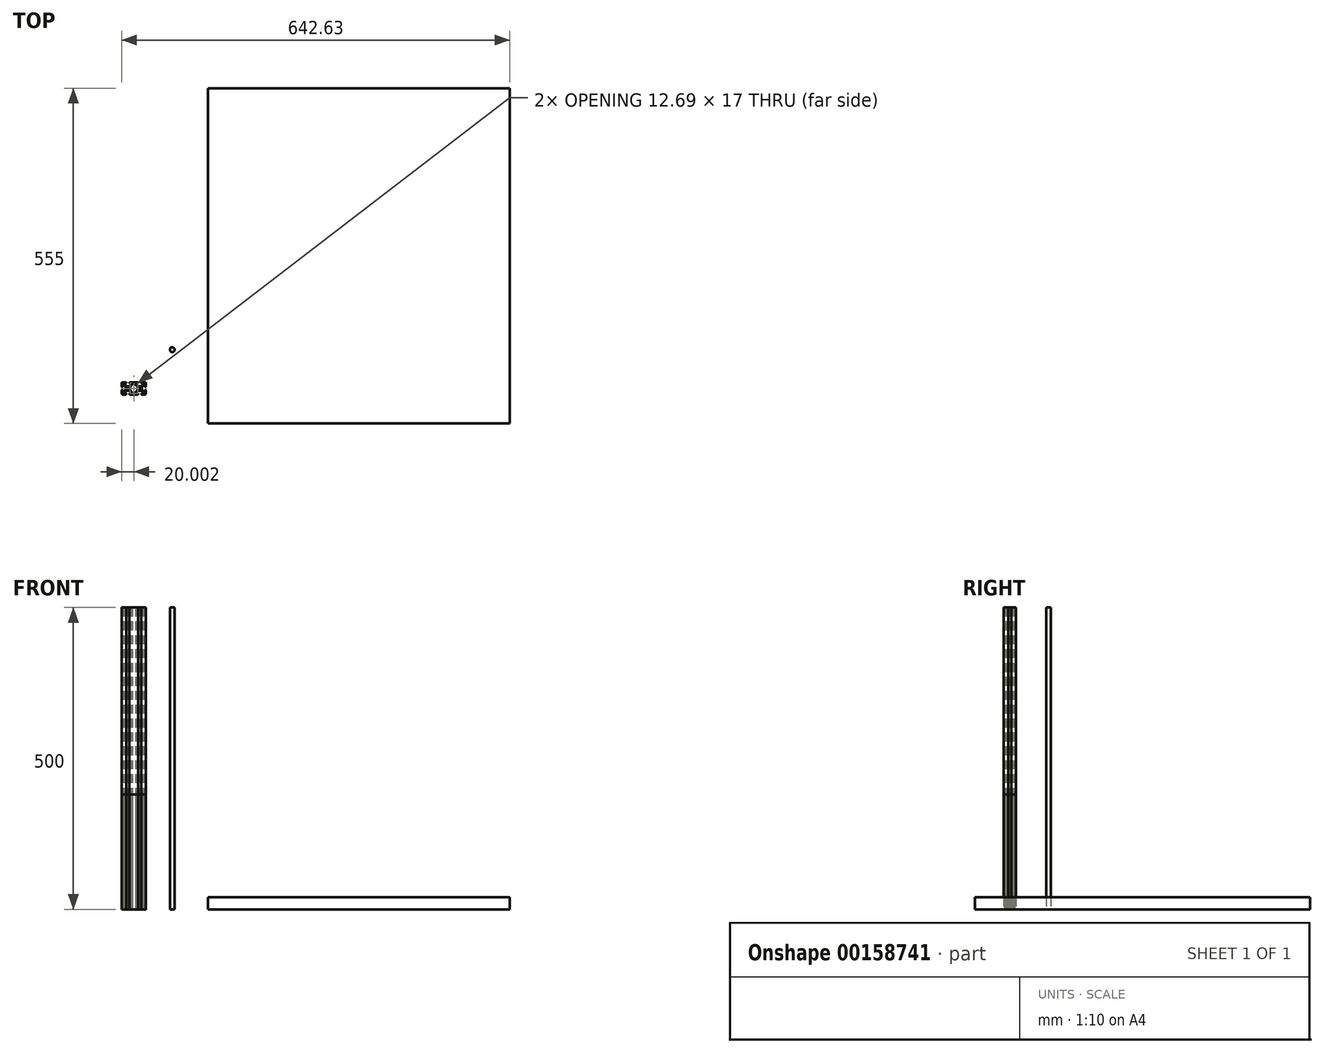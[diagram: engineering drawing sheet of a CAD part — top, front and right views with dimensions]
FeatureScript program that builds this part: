
annotation { "Feature Type Name" : "Feature", "Feature Type Description" : "" }
export const myFeature = defineFeature(function(context is Context, id is Id, definition is map)
    precondition{}
    {
        {
            var Q0;
            Q0=qCreatedBy(makeId("Top.planeOp"),FACE);
            var sketch = newSketch(context, id + "F0", { "sketchPlane" : qUnion([Q0])});
            skArc(sketch, "E0", {"start": v(-82.2, -54.18) * mm, "mid": v(-83.27, -54.62) * mm, "end": v(-83.7, -55.68) * mm});
            skLineSegment(sketch, "E1", {"start": v(-82.2, -54.18) * mm, "end": v(-76.85, -54.18) * mm});
            skArc(sketch, "E2", {"start": v(-76.34, -54.7) * mm, "mid": v(-76.49, -54.33) * mm, "end": v(-76.85, -54.18) * mm});
            skLineSegment(sketch, "E3", {"start": v(-76.34, -54.7) * mm, "end": v(-76.34, -55.18) * mm});
            skArc(sketch, "E4", {"start": v(-76.85, -55.68) * mm, "mid": v(-76.49, -55.54) * mm, "end": v(-76.34, -55.18) * mm});
            skLineSegment(sketch, "E5", {"start": v(-76.85, -55.68) * mm, "end": v(-79.2, -55.68) * mm});
            skLineSegment(sketch, "E6", {"start": v(-79.7, -56.2) * mm, "end": v(-79.7, -56.92) * mm});
            skLineSegment(sketch, "E7", {"start": v(-79.55, -57.28) * mm, "end": v(-76.45, -60.38) * mm});
            skLineSegment(sketch, "E8", {"start": v(-76.1, -60.53) * mm, "end": v(-71.32, -60.53) * mm});
            skLineSegment(sketch, "E9", {"start": v(-77.51, -61.44) * mm, "end": v(-80.61, -58.34) * mm});
            skLineSegment(sketch, "E10", {"start": v(-80.97, -58.19) * mm, "end": v(-81.7, -58.19) * mm});
            skLineSegment(sketch, "E11", {"start": v(-82.2, -58.7) * mm, "end": v(-82.2, -61.05) * mm});
            skLineSegment(sketch, "E12", {"start": v(-82.72, -61.55) * mm, "end": v(-83.2, -61.55) * mm});
            skLineSegment(sketch, "E13", {"start": v(-83.7, -61.05) * mm, "end": v(-83.7, -55.68) * mm});
            skArc(sketch, "E14", {"start": v(-79.2, -55.68) * mm, "mid": v(-79.55, -55.83) * mm, "end": v(-79.7, -56.2) * mm});
            skArc(sketch, "E15", {"start": v(-79.7, -56.92) * mm, "mid": v(-79.66, -57.11) * mm, "end": v(-79.55, -57.28) * mm});
            skArc(sketch, "E16", {"start": v(-80.61, -58.34) * mm, "mid": v(-80.78, -58.23) * mm, "end": v(-80.97, -58.19) * mm});
            skArc(sketch, "E17", {"start": v(-81.7, -58.19) * mm, "mid": v(-82.06, -58.34) * mm, "end": v(-82.2, -58.7) * mm});
            skArc(sketch, "E18", {"start": v(-82.72, -61.55) * mm, "mid": v(-82.36, -61.4) * mm, "end": v(-82.2, -61.05) * mm});
            skArc(sketch, "E19", {"start": v(-83.7, -61.05) * mm, "mid": v(-83.56, -61.4) * mm, "end": v(-83.2, -61.55) * mm});
            skLineSegment(sketch, "E20", {"start": v(-77.36, -61.8) * mm, "end": v(-77.36, -66.57) * mm});
            skLineSegment(sketch, "E21", {"start": v(-77.51, -66.93) * mm, "end": v(-80.61, -70.03) * mm});
            skLineSegment(sketch, "E22", {"start": v(-80.97, -70.18) * mm, "end": v(-81.7, -70.18) * mm});
            skLineSegment(sketch, "E23", {"start": v(-82.2, -69.67) * mm, "end": v(-82.2, -67.32) * mm});
            skLineSegment(sketch, "E24", {"start": v(-76.1, -67.84) * mm, "end": v(-71.32, -67.84) * mm});
            skLineSegment(sketch, "E25", {"start": v(-70.96, -67.99) * mm, "end": v(-67.86, -71.1) * mm});
            skLineSegment(sketch, "E26", {"start": v(-68.22, -72.68) * mm, "end": v(-70.57, -72.68) * mm});
            skLineSegment(sketch, "E27", {"start": v(-76.85, -72.68) * mm, "end": v(-79.2, -72.68) * mm});
            skLineSegment(sketch, "E28", {"start": v(-79.7, -71.45) * mm, "end": v(-79.7, -72.18) * mm});
            skLineSegment(sketch, "E29", {"start": v(-79.55, -71.1) * mm, "end": v(-76.45, -67.99) * mm});
            skLineSegment(sketch, "E30", {"start": v(-82.2, -74.18) * mm, "end": v(-76.85, -74.18) * mm});
            skLineSegment(sketch, "E31", {"start": v(-83.7, -72.68) * mm, "end": v(-83.7, -67.32) * mm});
            skLineSegment(sketch, "E32", {"start": v(-83.2, -66.81) * mm, "end": v(-82.72, -66.81) * mm});
            skLineSegment(sketch, "E33", {"start": v(-70.96, -60.38) * mm, "end": v(-67.86, -57.28) * mm});
            skLineSegment(sketch, "E34", {"start": v(-68.22, -55.68) * mm, "end": v(-70.57, -55.68) * mm});
            skLineSegment(sketch, "E35", {"start": v(-67.71, -56.2) * mm, "end": v(-67.71, -56.92) * mm});
            skLineSegment(sketch, "E36", {"start": v(-71.08, -55.18) * mm, "end": v(-71.08, -54.7) * mm});
            skLineSegment(sketch, "E37", {"start": v(-70.57, -54.18) * mm, "end": v(-63.7, -54.18) * mm});
            skPoint(sketch, "E37.endSnap0", {"position": v(-63.7, -54.18) * mm});
            skLineSegment(sketch, "E38", {"start": v(-69.9, -61.44) * mm, "end": v(-66.36, -57.9) * mm});
            skLineSegment(sketch, "E39", {"start": v(-66.21, -56.2) * mm, "end": v(-66.21, -57.54) * mm});
            skLineSegment(sketch, "E40", {"start": v(-65.7, -55.68) * mm, "end": v(-63.7, -55.68) * mm});
            skLineSegment(sketch, "E41", {"start": v(-70.05, -61.8) * mm, "end": v(-70.05, -66.57) * mm});
            skLineSegment(sketch, "E42", {"start": v(-69.9, -66.93) * mm, "end": v(-66.36, -70.47) * mm});
            skLineSegment(sketch, "E43", {"start": v(-66.21, -70.83) * mm, "end": v(-66.21, -72.18) * mm});
            skLineSegment(sketch, "E44", {"start": v(-71.08, -73.68) * mm, "end": v(-71.08, -73.2) * mm});
            skLineSegment(sketch, "E45", {"start": v(-70.57, -74.18) * mm, "end": v(-63.7, -74.18) * mm});
            skArc(sketch, "E46", {"start": v(-70.57, -54.18) * mm, "mid": v(-70.93, -54.33) * mm, "end": v(-71.08, -54.7) * mm});
            skArc(sketch, "E47", {"start": v(-71.08, -55.18) * mm, "mid": v(-70.93, -55.54) * mm, "end": v(-70.57, -55.68) * mm});
            skArc(sketch, "E48", {"start": v(-67.71, -56.2) * mm, "mid": v(-67.86, -55.83) * mm, "end": v(-68.22, -55.68) * mm});
            skArc(sketch, "E49", {"start": v(-67.86, -57.28) * mm, "mid": v(-67.75, -57.11) * mm, "end": v(-67.71, -56.92) * mm});
            skArc(sketch, "E50", {"start": v(-71.32, -60.53) * mm, "mid": v(-71.13, -60.5) * mm, "end": v(-70.96, -60.38) * mm});
            skArc(sketch, "E51", {"start": v(-76.45, -60.38) * mm, "mid": v(-76.29, -60.5) * mm, "end": v(-76.1, -60.53) * mm});
            skArc(sketch, "E52", {"start": v(-77.36, -61.8) * mm, "mid": v(-77.4, -61.6) * mm, "end": v(-77.51, -61.44) * mm});
            skArc(sketch, "E53", {"start": v(-65.7, -55.68) * mm, "mid": v(-66.06, -55.83) * mm, "end": v(-66.21, -56.2) * mm});
            skArc(sketch, "E54", {"start": v(-66.36, -57.9) * mm, "mid": v(-66.25, -57.73) * mm, "end": v(-66.21, -57.54) * mm});
            skArc(sketch, "E55", {"start": v(-83.2, -66.81) * mm, "mid": v(-83.56, -66.96) * mm, "end": v(-83.7, -67.32) * mm});
            skArc(sketch, "E56", {"start": v(-82.2, -67.32) * mm, "mid": v(-82.36, -66.96) * mm, "end": v(-82.72, -66.81) * mm});
            skArc(sketch, "E57", {"start": v(-82.2, -69.67) * mm, "mid": v(-82.06, -70.03) * mm, "end": v(-81.7, -70.18) * mm});
            skArc(sketch, "E58", {"start": v(-80.97, -70.18) * mm, "mid": v(-80.78, -70.14) * mm, "end": v(-80.61, -70.03) * mm});
            skArc(sketch, "E59", {"start": v(-79.55, -71.1) * mm, "mid": v(-79.66, -71.26) * mm, "end": v(-79.7, -71.45) * mm});
            skArc(sketch, "E60", {"start": v(-76.1, -67.84) * mm, "mid": v(-76.29, -67.88) * mm, "end": v(-76.45, -67.99) * mm});
            skArc(sketch, "E61", {"start": v(-77.51, -66.93) * mm, "mid": v(-77.4, -66.76) * mm, "end": v(-77.36, -66.57) * mm});
            skArc(sketch, "E62", {"start": v(-83.7, -72.68) * mm, "mid": v(-83.27, -73.74) * mm, "end": v(-82.2, -74.18) * mm});
            skArc(sketch, "E63", {"start": v(-76.85, -74.18) * mm, "mid": v(-76.49, -74.04) * mm, "end": v(-76.34, -73.68) * mm});
            skArc(sketch, "E64", {"start": v(-79.7, -72.18) * mm, "mid": v(-79.55, -72.54) * mm, "end": v(-79.2, -72.68) * mm});
            skArc(sketch, "E65", {"start": v(-76.34, -73.2) * mm, "mid": v(-76.49, -72.83) * mm, "end": v(-76.85, -72.68) * mm});
            skLineSegment(sketch, "E66", {"start": v(-76.34, -73.2) * mm, "end": v(-76.34, -73.68) * mm});
            skArc(sketch, "E67", {"start": v(-70.57, -72.68) * mm, "mid": v(-70.93, -72.83) * mm, "end": v(-71.08, -73.2) * mm});
            skArc(sketch, "E68", {"start": v(-71.08, -73.68) * mm, "mid": v(-70.93, -74.04) * mm, "end": v(-70.57, -74.18) * mm});
            skArc(sketch, "E69", {"start": v(-67.71, -71.45) * mm, "mid": v(-67.75, -71.26) * mm, "end": v(-67.86, -71.1) * mm});
            skArc(sketch, "E70", {"start": v(-68.22, -72.68) * mm, "mid": v(-67.86, -72.54) * mm, "end": v(-67.71, -72.18) * mm});
            skLineSegment(sketch, "E71", {"start": v(-67.71, -71.45) * mm, "end": v(-67.71, -72.18) * mm});
            skArc(sketch, "E72", {"start": v(-66.21, -70.83) * mm, "mid": v(-66.25, -70.63) * mm, "end": v(-66.36, -70.47) * mm});
            skArc(sketch, "E73", {"start": v(-66.21, -72.18) * mm, "mid": v(-66.06, -72.54) * mm, "end": v(-65.7, -72.68) * mm});
            skLineSegment(sketch, "E74", {"start": v(-63.7, -72.68) * mm, "end": v(-65.7, -72.68) * mm});
            skArc(sketch, "E75", {"start": v(-70.96, -67.99) * mm, "mid": v(-71.13, -67.88) * mm, "end": v(-71.32, -67.84) * mm});
            skArc(sketch, "E76", {"start": v(-70.05, -66.57) * mm, "mid": v(-70.01, -66.76) * mm, "end": v(-69.9, -66.93) * mm});
            skArc(sketch, "E77", {"start": v(-76.01, -62.06) * mm, "mid": v(-76.21, -62.83) * mm, "end": v(-75.64, -63.38) * mm});
            skArc(sketch, "E78", {"start": v(-74.51, -62.25) * mm, "mid": v(-75.06, -61.68) * mm, "end": v(-75.83, -61.88) * mm});
            skArc(sketch, "E79", {"start": v(-72.9, -62.25) * mm, "mid": v(-73.7, -62.09) * mm, "end": v(-74.51, -62.25) * mm});
            skLineSegment(sketch, "E80", {"start": v(-76.01, -62.06) * mm, "end": v(-75.83, -61.88) * mm});
            skArc(sketch, "E81.1.0", {"start": v(-75.83, -66.49) * mm, "mid": v(-75.06, -66.7) * mm, "end": v(-74.51, -66.12) * mm});
            skArc(sketch, "E81.1.1", {"start": v(-75.64, -63.38) * mm, "mid": v(-75.8, -64.18) * mm, "end": v(-75.64, -64.99) * mm});
            skArc(sketch, "E81.1.2", {"start": v(-75.64, -64.99) * mm, "mid": v(-76.21, -65.54) * mm, "end": v(-76.01, -66.3) * mm});
            skLineSegment(sketch, "E81.1.3", {"start": v(-75.83, -66.49) * mm, "end": v(-76.01, -66.3) * mm});
            skArc(sketch, "E81.2.0", {"start": v(-71.4, -66.3) * mm, "mid": v(-71.2, -65.54) * mm, "end": v(-71.77, -64.99) * mm});
            skArc(sketch, "E81.2.1", {"start": v(-74.51, -66.12) * mm, "mid": v(-73.7, -66.28) * mm, "end": v(-72.9, -66.12) * mm});
            skArc(sketch, "E81.2.2", {"start": v(-72.9, -66.12) * mm, "mid": v(-72.35, -66.7) * mm, "end": v(-71.58, -66.49) * mm});
            skLineSegment(sketch, "E81.2.3", {"start": v(-71.4, -66.3) * mm, "end": v(-71.58, -66.49) * mm});
            skArc(sketch, "E81.3.0", {"start": v(-71.58, -61.88) * mm, "mid": v(-72.35, -61.68) * mm, "end": v(-72.9, -62.25) * mm});
            skArc(sketch, "E81.3.1", {"start": v(-71.77, -64.99) * mm, "mid": v(-71.61, -64.18) * mm, "end": v(-71.77, -63.38) * mm});
            skArc(sketch, "E81.3.2", {"start": v(-71.77, -63.38) * mm, "mid": v(-71.2, -62.83) * mm, "end": v(-71.4, -62.06) * mm});
            skLineSegment(sketch, "E81.3.3", {"start": v(-71.58, -61.88) * mm, "end": v(-71.4, -62.06) * mm});
            skLineSegment(sketch, "E82.MirrorCS", {"start": v(-51.08, -73.2) * mm, "end": v(-51.08, -73.68) * mm});
            skLineSegment(sketch, "E83.MirrorCS", {"start": v(-56.01, -66.3) * mm, "end": v(-55.83, -66.49) * mm});
            skLineSegment(sketch, "E84.MirrorCS", {"start": v(-51.4, -62.06) * mm, "end": v(-51.58, -61.88) * mm});
            skLineSegment(sketch, "E85.MirrorCS", {"start": v(-59.7, -71.45) * mm, "end": v(-59.7, -72.18) * mm});
            skArc(sketch, "E86.MirrorCS", {"start": v(-54.51, -66.12) * mm, "mid": v(-55.06, -66.7) * mm, "end": v(-55.83, -66.49) * mm});
            skLineSegment(sketch, "E87.MirrorCS", {"start": v(-47.71, -56.2) * mm, "end": v(-47.71, -56.92) * mm});
            skLineSegment(sketch, "E88.MirrorCS", {"start": v(-51.08, -54.7) * mm, "end": v(-51.08, -55.18) * mm});
            skArc(sketch, "E89.MirrorCS", {"start": v(-51.08, -54.7) * mm, "mid": v(-50.93, -54.33) * mm, "end": v(-50.57, -54.18) * mm});
            skArc(sketch, "E90.MirrorCS", {"start": v(-47.71, -56.92) * mm, "mid": v(-47.75, -57.11) * mm, "end": v(-47.86, -57.28) * mm});
            skArc(sketch, "E91.MirrorCS", {"start": v(-59.2, -72.68) * mm, "mid": v(-59.55, -72.54) * mm, "end": v(-59.7, -72.18) * mm});
            skArc(sketch, "E92.MirrorCS", {"start": v(-50.57, -74.18) * mm, "mid": v(-50.93, -74.04) * mm, "end": v(-51.08, -73.68) * mm});
            skArc(sketch, "E93.MirrorCS", {"start": v(-61.71, -55.68) * mm, "mid": v(-61.35, -55.83) * mm, "end": v(-61.2, -56.2) * mm});
            skArc(sketch, "E94.MirrorCS", {"start": v(-59.7, -71.45) * mm, "mid": v(-59.66, -71.26) * mm, "end": v(-59.55, -71.1) * mm});
            skArc(sketch, "E95.MirrorCS", {"start": v(-56.01, -66.3) * mm, "mid": v(-56.21, -65.54) * mm, "end": v(-55.64, -64.99) * mm});
            skLineSegment(sketch, "E96.MirrorCS", {"start": v(-55.83, -61.88) * mm, "end": v(-56.01, -62.06) * mm});
            skLineSegment(sketch, "E97.MirrorCS", {"start": v(-56.34, -73.68) * mm, "end": v(-56.34, -73.2) * mm});
            skArc(sketch, "E98.MirrorCS", {"start": v(-56.34, -73.68) * mm, "mid": v(-56.49, -74.04) * mm, "end": v(-56.85, -74.18) * mm});
            skArc(sketch, "E99.MirrorCS", {"start": v(-56.45, -67.99) * mm, "mid": v(-56.29, -67.88) * mm, "end": v(-56.1, -67.84) * mm});
            skLineSegment(sketch, "E100.MirrorCS", {"start": v(-59.2, -55.68) * mm, "end": v(-56.85, -55.68) * mm});
            skArc(sketch, "E101.MirrorCS", {"start": v(-56.1, -60.53) * mm, "mid": v(-56.29, -60.5) * mm, "end": v(-56.45, -60.38) * mm});
            skArc(sketch, "E102.MirrorCS", {"start": v(-51.77, -63.38) * mm, "mid": v(-51.61, -64.18) * mm, "end": v(-51.77, -64.99) * mm});
            skArc(sketch, "E103.MirrorCS", {"start": v(-44.7, -61.55) * mm, "mid": v(-45.06, -61.4) * mm, "end": v(-45.2, -61.05) * mm});
            skArc(sketch, "E104.MirrorCS", {"start": v(-61.2, -72.18) * mm, "mid": v(-61.35, -72.54) * mm, "end": v(-61.71, -72.68) * mm});
            skArc(sketch, "E105.MirrorCS", {"start": v(-55.83, -61.88) * mm, "mid": v(-55.06, -61.68) * mm, "end": v(-54.51, -62.25) * mm});
            skArc(sketch, "E106.MirrorCS", {"start": v(-45.2, -69.67) * mm, "mid": v(-45.36, -70.03) * mm, "end": v(-45.72, -70.18) * mm});
            skArc(sketch, "E107.MirrorCS", {"start": v(-59.55, -57.28) * mm, "mid": v(-59.66, -57.11) * mm, "end": v(-59.7, -56.92) * mm});
            skArc(sketch, "E108.MirrorCS", {"start": v(-51.08, -73.2) * mm, "mid": v(-50.93, -72.83) * mm, "end": v(-50.57, -72.68) * mm});
            skArc(sketch, "E109.MirrorCS", {"start": v(-51.58, -66.49) * mm, "mid": v(-52.35, -66.7) * mm, "end": v(-52.9, -66.12) * mm});
            skArc(sketch, "E110.MirrorCS", {"start": v(-45.72, -58.19) * mm, "mid": v(-45.36, -58.34) * mm, "end": v(-45.2, -58.7) * mm});
            skArc(sketch, "E111.MirrorCS", {"start": v(-61.2, -70.83) * mm, "mid": v(-61.16, -70.63) * mm, "end": v(-61.05, -70.47) * mm});
            skLineSegment(sketch, "E112.MirrorCS", {"start": v(-61.71, -55.68) * mm, "end": v(-63.7, -55.68) * mm});
            skArc(sketch, "E113.MirrorCS", {"start": v(-45.2, -67.32) * mm, "mid": v(-45.06, -66.96) * mm, "end": v(-44.7, -66.81) * mm});
            skLineSegment(sketch, "E114.MirrorCS", {"start": v(-44.22, -66.81) * mm, "end": v(-44.7, -66.81) * mm});
            skArc(sketch, "E115.MirrorCS", {"start": v(-59.7, -56.2) * mm, "mid": v(-59.55, -55.83) * mm, "end": v(-59.2, -55.68) * mm});
            skArc(sketch, "E116.MirrorCS", {"start": v(-47.71, -72.18) * mm, "mid": v(-47.86, -72.54) * mm, "end": v(-48.22, -72.68) * mm});
            skArc(sketch, "E117.MirrorCS", {"start": v(-46.8, -58.34) * mm, "mid": v(-46.64, -58.23) * mm, "end": v(-46.44, -58.19) * mm});
            skLineSegment(sketch, "E118.MirrorCS", {"start": v(-45.2, -69.67) * mm, "end": v(-45.2, -67.32) * mm});
            skLineSegment(sketch, "E119.MirrorCS", {"start": v(-61.2, -56.2) * mm, "end": v(-61.2, -57.54) * mm});
            skArc(sketch, "E120.MirrorCS", {"start": v(-44.22, -66.81) * mm, "mid": v(-43.86, -66.96) * mm, "end": v(-43.7, -67.32) * mm});
            skLineSegment(sketch, "E121.MirrorCS", {"start": v(-44.7, -61.55) * mm, "end": v(-44.22, -61.55) * mm});
            skLineSegment(sketch, "E122.MirrorCS", {"start": v(-46.44, -58.19) * mm, "end": v(-45.72, -58.19) * mm});
            skArc(sketch, "E123.MirrorCS", {"start": v(-50.57, -55.68) * mm, "mid": v(-50.93, -55.54) * mm, "end": v(-51.08, -55.18) * mm});
            skArc(sketch, "E124.MirrorCS", {"start": v(-45.2, -54.18) * mm, "mid": v(-44.15, -54.62) * mm, "end": v(-43.7, -55.68) * mm});
            skArc(sketch, "E125.MirrorCS", {"start": v(-48.22, -55.68) * mm, "mid": v(-47.86, -55.83) * mm, "end": v(-47.71, -56.2) * mm});
            skArc(sketch, "E126.MirrorCS", {"start": v(-61.05, -57.9) * mm, "mid": v(-61.16, -57.73) * mm, "end": v(-61.2, -57.54) * mm});
            skArc(sketch, "E127.MirrorCS", {"start": v(-56.34, -55.18) * mm, "mid": v(-56.49, -55.54) * mm, "end": v(-56.85, -55.68) * mm});
            skArc(sketch, "E128.MirrorCS", {"start": v(-54.51, -62.25) * mm, "mid": v(-53.7, -62.09) * mm, "end": v(-52.9, -62.25) * mm});
            skArc(sketch, "E129.MirrorCS", {"start": v(-52.9, -66.12) * mm, "mid": v(-53.7, -66.28) * mm, "end": v(-54.51, -66.12) * mm});
            skLineSegment(sketch, "E130.MirrorCS", {"start": v(-46.44, -70.18) * mm, "end": v(-45.72, -70.18) * mm});
            skArc(sketch, "E131.MirrorCS", {"start": v(-56.85, -54.18) * mm, "mid": v(-56.49, -54.33) * mm, "end": v(-56.34, -54.7) * mm});
            skArc(sketch, "E132.MirrorCS", {"start": v(-43.7, -72.68) * mm, "mid": v(-44.15, -73.74) * mm, "end": v(-45.2, -74.18) * mm});
            skArc(sketch, "E133.MirrorCS", {"start": v(-52.9, -62.25) * mm, "mid": v(-52.35, -61.68) * mm, "end": v(-51.58, -61.88) * mm});
            skArc(sketch, "E134.MirrorCS", {"start": v(-57.36, -66.57) * mm, "mid": v(-57.4, -66.76) * mm, "end": v(-57.51, -66.93) * mm});
            skLineSegment(sketch, "E135.MirrorCS", {"start": v(-47.71, -71.45) * mm, "end": v(-47.71, -72.18) * mm});
            skArc(sketch, "E136.MirrorCS", {"start": v(-51.32, -67.84) * mm, "mid": v(-51.13, -67.88) * mm, "end": v(-50.96, -67.99) * mm});
            skLineSegment(sketch, "E137.MirrorCS", {"start": v(-56.34, -55.18) * mm, "end": v(-56.34, -54.7) * mm});
            skArc(sketch, "E138.MirrorCS", {"start": v(-50.05, -61.8) * mm, "mid": v(-50.01, -61.6) * mm, "end": v(-49.9, -61.44) * mm});
            skArc(sketch, "E139.MirrorCS", {"start": v(-49.9, -66.93) * mm, "mid": v(-50.01, -66.76) * mm, "end": v(-50.05, -66.57) * mm});
            skLineSegment(sketch, "E140.MirrorCS", {"start": v(-51.58, -66.49) * mm, "end": v(-51.4, -66.3) * mm});
            skArc(sketch, "E141.MirrorCS", {"start": v(-51.4, -62.06) * mm, "mid": v(-51.2, -62.83) * mm, "end": v(-51.77, -63.38) * mm});
            skArc(sketch, "E142.MirrorCS", {"start": v(-55.64, -63.38) * mm, "mid": v(-56.21, -62.83) * mm, "end": v(-56.01, -62.06) * mm});
            skLineSegment(sketch, "E143.MirrorCS", {"start": v(-61.2, -70.83) * mm, "end": v(-61.2, -72.18) * mm});
            skArc(sketch, "E144.MirrorCS", {"start": v(-47.86, -71.1) * mm, "mid": v(-47.75, -71.26) * mm, "end": v(-47.71, -71.45) * mm});
            skLineSegment(sketch, "E145.MirrorCS", {"start": v(-59.7, -56.2) * mm, "end": v(-59.7, -56.92) * mm});
            skArc(sketch, "E146.MirrorCS", {"start": v(-50.96, -60.38) * mm, "mid": v(-51.13, -60.5) * mm, "end": v(-51.32, -60.53) * mm});
            skArc(sketch, "E147.MirrorCS", {"start": v(-56.85, -72.68) * mm, "mid": v(-56.49, -72.83) * mm, "end": v(-56.34, -73.2) * mm});
            skArc(sketch, "E148.MirrorCS", {"start": v(-51.77, -64.99) * mm, "mid": v(-51.2, -65.54) * mm, "end": v(-51.4, -66.3) * mm});
            skArc(sketch, "E149.MirrorCS", {"start": v(-43.7, -61.05) * mm, "mid": v(-43.86, -61.4) * mm, "end": v(-44.22, -61.55) * mm});
            skLineSegment(sketch, "E150.MirrorCS", {"start": v(-63.7, -72.68) * mm, "end": v(-61.71, -72.68) * mm});
            skArc(sketch, "E151.MirrorCS", {"start": v(-55.64, -64.99) * mm, "mid": v(-55.8, -64.18) * mm, "end": v(-55.64, -63.38) * mm});
            skLineSegment(sketch, "E152.MirrorCS", {"start": v(-59.2, -72.68) * mm, "end": v(-56.85, -72.68) * mm});
            skArc(sketch, "E153.MirrorCS", {"start": v(-46.44, -70.18) * mm, "mid": v(-46.64, -70.14) * mm, "end": v(-46.8, -70.03) * mm});
            skLineSegment(sketch, "E154.MirrorCS", {"start": v(-56.45, -67.99) * mm, "end": v(-59.55, -71.1) * mm});
            skLineSegment(sketch, "E155.MirrorCS", {"start": v(-57.36, -61.8) * mm, "end": v(-57.36, -66.57) * mm});
            skLineSegment(sketch, "E156.MirrorCS", {"start": v(-56.45, -60.38) * mm, "end": v(-59.55, -57.28) * mm});
            skLineSegment(sketch, "E157.MirrorCS", {"start": v(-51.32, -67.84) * mm, "end": v(-56.1, -67.84) * mm});
            skLineSegment(sketch, "E158.MirrorCS", {"start": v(-45.2, -58.7) * mm, "end": v(-45.2, -61.05) * mm});
            skLineSegment(sketch, "E159.MirrorCS", {"start": v(-49.9, -61.44) * mm, "end": v(-46.8, -58.34) * mm});
            skLineSegment(sketch, "E160.MirrorCS", {"start": v(-51.32, -60.53) * mm, "end": v(-56.1, -60.53) * mm});
            skLineSegment(sketch, "E161.MirrorCS", {"start": v(-47.86, -57.28) * mm, "end": v(-50.96, -60.38) * mm});
            skLineSegment(sketch, "E162.MirrorCS", {"start": v(-50.57, -55.68) * mm, "end": v(-48.22, -55.68) * mm});
            skLineSegment(sketch, "E163.MirrorCS", {"start": v(-45.2, -54.18) * mm, "end": v(-50.57, -54.18) * mm});
            skLineSegment(sketch, "E164.MirrorCS", {"start": v(-43.7, -61.05) * mm, "end": v(-43.7, -55.68) * mm});
            skLineSegment(sketch, "E165.MirrorCS", {"start": v(-57.51, -61.44) * mm, "end": v(-61.05, -57.9) * mm});
            skLineSegment(sketch, "E166.MirrorCS", {"start": v(-43.7, -72.68) * mm, "end": v(-43.7, -67.32) * mm});
            skLineSegment(sketch, "E167.MirrorCS", {"start": v(-56.85, -54.18) * mm, "end": v(-63.7, -54.18) * mm});
            skLineSegment(sketch, "E168.MirrorCS", {"start": v(-45.2, -74.18) * mm, "end": v(-50.57, -74.18) * mm});
            skLineSegment(sketch, "E169.MirrorCS", {"start": v(-49.9, -66.93) * mm, "end": v(-46.8, -70.03) * mm});
            skLineSegment(sketch, "E170.MirrorCS", {"start": v(-47.86, -71.1) * mm, "end": v(-50.96, -67.99) * mm});
            skLineSegment(sketch, "E171.MirrorCS", {"start": v(-56.85, -74.18) * mm, "end": v(-63.7, -74.18) * mm});
            skLineSegment(sketch, "E172.MirrorCS", {"start": v(-50.05, -61.8) * mm, "end": v(-50.05, -66.57) * mm});
            skLineSegment(sketch, "E173.MirrorCS", {"start": v(-50.57, -72.68) * mm, "end": v(-48.22, -72.68) * mm});
            skLineSegment(sketch, "E174.MirrorCS", {"start": v(-57.51, -66.93) * mm, "end": v(-61.05, -70.47) * mm});
            skArc(sketch, "E175", {"start": v(-69.9, -61.44) * mm, "mid": v(-70.01, -61.6) * mm, "end": v(-70.05, -61.8) * mm});
            skArc(sketch, "E176", {"start": v(-57.36, -61.8) * mm, "mid": v(-57.4, -61.6) * mm, "end": v(-57.51, -61.44) * mm});
            skCircle(sketch, "E177", {"center": v(0, 0) * mm, "radius": 4 * mm});
            skArc(sketch, "E178", {"start": v(-19.39, -61.83) * mm, "mid": v(-20.45, -62.27) * mm, "end": v(-20.89, -63.33) * mm});
            skLineSegment(sketch, "E179", {"start": v(-19.39, -61.83) * mm, "end": v(-14.03, -61.83) * mm});
            skArc(sketch, "E180", {"start": v(-13.52, -62.34) * mm, "mid": v(-13.67, -61.98) * mm, "end": v(-14.03, -61.83) * mm});
            skLineSegment(sketch, "E181", {"start": v(-13.52, -62.34) * mm, "end": v(-13.52, -62.83) * mm});
            skArc(sketch, "E182", {"start": v(-14.03, -63.33) * mm, "mid": v(-13.67, -63.19) * mm, "end": v(-13.52, -62.83) * mm});
            skLineSegment(sketch, "E183", {"start": v(-14.03, -63.33) * mm, "end": v(-16.37, -63.33) * mm});
            skLineSegment(sketch, "E184", {"start": v(-16.88, -63.84) * mm, "end": v(-16.88, -64.57) * mm});
            skLineSegment(sketch, "E185", {"start": v(-16.73, -64.93) * mm, "end": v(-13.63, -68.03) * mm});
            skLineSegment(sketch, "E186", {"start": v(-13.27, -68.18) * mm, "end": v(-8.5, -68.18) * mm});
            skLineSegment(sketch, "E187", {"start": v(-14.7, -69.1) * mm, "end": v(-17.8, -65.99) * mm});
            skLineSegment(sketch, "E188", {"start": v(-18.15, -65.84) * mm, "end": v(-18.88, -65.84) * mm});
            skLineSegment(sketch, "E189", {"start": v(-19.39, -66.35) * mm, "end": v(-19.39, -68.7) * mm});
            skLineSegment(sketch, "E190", {"start": v(-19.9, -69.2) * mm, "end": v(-20.38, -69.2) * mm});
            skLineSegment(sketch, "E191", {"start": v(-20.89, -68.7) * mm, "end": v(-20.89, -63.33) * mm});
            skArc(sketch, "E192", {"start": v(-16.37, -63.33) * mm, "mid": v(-16.73, -63.48) * mm, "end": v(-16.88, -63.84) * mm});
            skArc(sketch, "E193", {"start": v(-16.88, -64.57) * mm, "mid": v(-16.84, -64.76) * mm, "end": v(-16.73, -64.93) * mm});
            skArc(sketch, "E194", {"start": v(-17.8, -65.99) * mm, "mid": v(-17.96, -65.88) * mm, "end": v(-18.15, -65.84) * mm});
            skArc(sketch, "E195", {"start": v(-18.88, -65.84) * mm, "mid": v(-19.24, -65.99) * mm, "end": v(-19.39, -66.35) * mm});
            skArc(sketch, "E196", {"start": v(-19.9, -69.2) * mm, "mid": v(-19.54, -69.06) * mm, "end": v(-19.39, -68.7) * mm});
            skArc(sketch, "E197", {"start": v(-20.89, -68.7) * mm, "mid": v(-20.74, -69.06) * mm, "end": v(-20.38, -69.2) * mm});
            skLineSegment(sketch, "E198", {"start": v(-14.54, -69.45) * mm, "end": v(-14.54, -74.22) * mm});
            skLineSegment(sketch, "E199", {"start": v(-14.7, -74.58) * mm, "end": v(-17.8, -77.68) * mm});
            skLineSegment(sketch, "E200", {"start": v(-18.15, -77.83) * mm, "end": v(-18.88, -77.83) * mm});
            skLineSegment(sketch, "E201", {"start": v(-19.39, -77.32) * mm, "end": v(-19.39, -74.97) * mm});
            skLineSegment(sketch, "E202", {"start": v(-13.27, -75.49) * mm, "end": v(-8.5, -75.49) * mm});
            skLineSegment(sketch, "E203", {"start": v(-8.14, -75.64) * mm, "end": v(-5.04, -78.74) * mm});
            skLineSegment(sketch, "E204", {"start": v(-5.4, -80.33) * mm, "end": v(-7.75, -80.33) * mm});
            skLineSegment(sketch, "E205", {"start": v(-14.03, -80.33) * mm, "end": v(-16.37, -80.33) * mm});
            skLineSegment(sketch, "E206", {"start": v(-16.88, -79.1) * mm, "end": v(-16.88, -79.83) * mm});
            skLineSegment(sketch, "E207", {"start": v(-16.73, -78.74) * mm, "end": v(-13.63, -75.64) * mm});
            skLineSegment(sketch, "E208", {"start": v(-19.39, -81.83) * mm, "end": v(-14.03, -81.83) * mm});
            skLineSegment(sketch, "E209", {"start": v(-20.89, -80.33) * mm, "end": v(-20.89, -74.97) * mm});
            skLineSegment(sketch, "E210", {"start": v(-20.38, -74.46) * mm, "end": v(-19.9, -74.46) * mm});
            skLineSegment(sketch, "E211", {"start": v(-8.14, -68.03) * mm, "end": v(-5.04, -64.93) * mm});
            skLineSegment(sketch, "E212", {"start": v(-5.4, -63.33) * mm, "end": v(-7.75, -63.33) * mm});
            skLineSegment(sketch, "E213", {"start": v(-4.9, -63.84) * mm, "end": v(-4.9, -64.57) * mm});
            skLineSegment(sketch, "E214", {"start": v(-8.26, -62.83) * mm, "end": v(-8.26, -62.34) * mm});
            skLineSegment(sketch, "E215", {"start": v(-7.75, -61.83) * mm, "end": v(-0.89, -61.83) * mm});
            skPoint(sketch, "E215.endSnap0", {"position": v(-0.89, -61.83) * mm});
            skLineSegment(sketch, "E216", {"start": v(-7.08, -69.1) * mm, "end": v(-3.54, -65.55) * mm});
            skLineSegment(sketch, "E217", {"start": v(-3.4, -63.84) * mm, "end": v(-3.4, -65.2) * mm});
            skLineSegment(sketch, "E218", {"start": v(-2.88, -63.33) * mm, "end": v(-0.89, -63.33) * mm});
            skLineSegment(sketch, "E219", {"start": v(-7.23, -69.45) * mm, "end": v(-7.23, -74.22) * mm});
            skLineSegment(sketch, "E220", {"start": v(-7.08, -74.58) * mm, "end": v(-3.54, -78.12) * mm});
            skLineSegment(sketch, "E221", {"start": v(-3.4, -78.48) * mm, "end": v(-3.4, -79.83) * mm});
            skLineSegment(sketch, "E222", {"start": v(-8.26, -81.33) * mm, "end": v(-8.26, -80.84) * mm});
            skLineSegment(sketch, "E223", {"start": v(-7.75, -81.83) * mm, "end": v(-0.89, -81.83) * mm});
            skArc(sketch, "E224", {"start": v(-7.75, -61.83) * mm, "mid": v(-8.1, -61.98) * mm, "end": v(-8.26, -62.34) * mm});
            skArc(sketch, "E225", {"start": v(-8.26, -62.83) * mm, "mid": v(-8.1, -63.19) * mm, "end": v(-7.75, -63.33) * mm});
            skArc(sketch, "E226", {"start": v(-4.9, -63.84) * mm, "mid": v(-5.04, -63.48) * mm, "end": v(-5.4, -63.33) * mm});
            skArc(sketch, "E227", {"start": v(-5.04, -64.93) * mm, "mid": v(-4.93, -64.76) * mm, "end": v(-4.9, -64.57) * mm});
            skArc(sketch, "E228", {"start": v(-8.5, -68.18) * mm, "mid": v(-8.3, -68.14) * mm, "end": v(-8.14, -68.03) * mm});
            skArc(sketch, "E229", {"start": v(-13.63, -68.03) * mm, "mid": v(-13.47, -68.14) * mm, "end": v(-13.27, -68.18) * mm});
            skArc(sketch, "E230", {"start": v(-14.54, -69.45) * mm, "mid": v(-14.58, -69.26) * mm, "end": v(-14.7, -69.1) * mm});
            skArc(sketch, "E231", {"start": v(-2.88, -63.33) * mm, "mid": v(-3.24, -63.48) * mm, "end": v(-3.4, -63.84) * mm});
            skArc(sketch, "E232", {"start": v(-3.54, -65.55) * mm, "mid": v(-3.43, -65.38) * mm, "end": v(-3.4, -65.2) * mm});
            skArc(sketch, "E233", {"start": v(-20.38, -74.46) * mm, "mid": v(-20.74, -74.61) * mm, "end": v(-20.89, -74.97) * mm});
            skArc(sketch, "E234", {"start": v(-19.39, -74.97) * mm, "mid": v(-19.54, -74.61) * mm, "end": v(-19.9, -74.46) * mm});
            skArc(sketch, "E235", {"start": v(-19.39, -77.32) * mm, "mid": v(-19.24, -77.68) * mm, "end": v(-18.88, -77.83) * mm});
            skArc(sketch, "E236", {"start": v(-18.15, -77.83) * mm, "mid": v(-17.96, -77.8) * mm, "end": v(-17.8, -77.68) * mm});
            skArc(sketch, "E237", {"start": v(-16.73, -78.74) * mm, "mid": v(-16.84, -78.9) * mm, "end": v(-16.88, -79.1) * mm});
            skArc(sketch, "E238", {"start": v(-13.27, -75.49) * mm, "mid": v(-13.47, -75.53) * mm, "end": v(-13.63, -75.64) * mm});
            skArc(sketch, "E239", {"start": v(-14.7, -74.58) * mm, "mid": v(-14.58, -74.41) * mm, "end": v(-14.54, -74.22) * mm});
            skArc(sketch, "E240", {"start": v(-20.89, -80.33) * mm, "mid": v(-20.45, -81.4) * mm, "end": v(-19.39, -81.83) * mm});
            skArc(sketch, "E241", {"start": v(-14.03, -81.83) * mm, "mid": v(-13.67, -81.69) * mm, "end": v(-13.52, -81.33) * mm});
            skArc(sketch, "E242", {"start": v(-16.88, -79.83) * mm, "mid": v(-16.73, -80.19) * mm, "end": v(-16.37, -80.33) * mm});
            skArc(sketch, "E243", {"start": v(-13.52, -80.84) * mm, "mid": v(-13.67, -80.48) * mm, "end": v(-14.03, -80.33) * mm});
            skLineSegment(sketch, "E244", {"start": v(-13.52, -80.84) * mm, "end": v(-13.52, -81.33) * mm});
            skArc(sketch, "E245", {"start": v(-7.75, -80.33) * mm, "mid": v(-8.1, -80.48) * mm, "end": v(-8.26, -80.84) * mm});
            skArc(sketch, "E246", {"start": v(-8.26, -81.33) * mm, "mid": v(-8.1, -81.69) * mm, "end": v(-7.75, -81.83) * mm});
            skArc(sketch, "E247", {"start": v(-4.9, -79.1) * mm, "mid": v(-4.93, -78.9) * mm, "end": v(-5.04, -78.74) * mm});
            skArc(sketch, "E248", {"start": v(-5.4, -80.33) * mm, "mid": v(-5.04, -80.19) * mm, "end": v(-4.9, -79.83) * mm});
            skLineSegment(sketch, "E249", {"start": v(-4.9, -79.1) * mm, "end": v(-4.9, -79.83) * mm});
            skArc(sketch, "E250", {"start": v(-3.4, -78.48) * mm, "mid": v(-3.43, -78.29) * mm, "end": v(-3.54, -78.12) * mm});
            skArc(sketch, "E251", {"start": v(-3.4, -79.83) * mm, "mid": v(-3.24, -80.19) * mm, "end": v(-2.88, -80.33) * mm});
            skLineSegment(sketch, "E252", {"start": v(-0.89, -80.33) * mm, "end": v(-2.88, -80.33) * mm});
            skArc(sketch, "E253", {"start": v(-8.14, -75.64) * mm, "mid": v(-8.3, -75.53) * mm, "end": v(-8.5, -75.49) * mm});
            skArc(sketch, "E254", {"start": v(-7.23, -74.22) * mm, "mid": v(-7.2, -74.41) * mm, "end": v(-7.08, -74.58) * mm});
            skArc(sketch, "E255", {"start": v(-13.2, -69.7) * mm, "mid": v(-13.4, -70.48) * mm, "end": v(-12.82, -71.03) * mm});
            skArc(sketch, "E256", {"start": v(-11.7, -69.9) * mm, "mid": v(-12.24, -69.33) * mm, "end": v(-13.01, -69.53) * mm});
            skArc(sketch, "E257", {"start": v(-10.08, -69.9) * mm, "mid": v(-10.89, -69.74) * mm, "end": v(-11.7, -69.9) * mm});
            skLineSegment(sketch, "E258", {"start": v(-13.2, -69.7) * mm, "end": v(-13.01, -69.53) * mm});
            skArc(sketch, "E259.1.0", {"start": v(-13.01, -74.14) * mm, "mid": v(-12.24, -74.34) * mm, "end": v(-11.7, -73.77) * mm});
            skArc(sketch, "E259.1.1", {"start": v(-12.82, -71.03) * mm, "mid": v(-12.98, -71.83) * mm, "end": v(-12.82, -72.64) * mm});
            skArc(sketch, "E259.1.2", {"start": v(-12.82, -72.64) * mm, "mid": v(-13.4, -73.2) * mm, "end": v(-13.2, -73.96) * mm});
            skLineSegment(sketch, "E259.1.3", {"start": v(-13.01, -74.14) * mm, "end": v(-13.2, -73.96) * mm});
            skArc(sketch, "E259.2.0", {"start": v(-8.58, -73.96) * mm, "mid": v(-8.38, -73.2) * mm, "end": v(-8.95, -72.64) * mm});
            skArc(sketch, "E259.2.1", {"start": v(-11.7, -73.77) * mm, "mid": v(-10.89, -73.93) * mm, "end": v(-10.08, -73.77) * mm});
            skArc(sketch, "E259.2.2", {"start": v(-10.08, -73.77) * mm, "mid": v(-9.53, -74.34) * mm, "end": v(-8.76, -74.14) * mm});
            skLineSegment(sketch, "E259.2.3", {"start": v(-8.58, -73.96) * mm, "end": v(-8.76, -74.14) * mm});
            skArc(sketch, "E259.3.0", {"start": v(-8.76, -69.53) * mm, "mid": v(-9.53, -69.33) * mm, "end": v(-10.08, -69.9) * mm});
            skArc(sketch, "E259.3.1", {"start": v(-8.95, -72.64) * mm, "mid": v(-8.8, -71.83) * mm, "end": v(-8.95, -71.03) * mm});
            skArc(sketch, "E259.3.2", {"start": v(-8.95, -71.03) * mm, "mid": v(-8.38, -70.48) * mm, "end": v(-8.58, -69.7) * mm});
            skLineSegment(sketch, "E259.3.3", {"start": v(-8.76, -69.53) * mm, "end": v(-8.58, -69.7) * mm});
            skLineSegment(sketch, "E260.MirrorCS", {"start": v(11.74, -80.84) * mm, "end": v(11.74, -81.33) * mm});
            skLineSegment(sketch, "E261.MirrorCS", {"start": v(6.8, -73.96) * mm, "end": v(6.99, -74.14) * mm});
            skLineSegment(sketch, "E262.MirrorCS", {"start": v(11.42, -69.7) * mm, "end": v(11.24, -69.53) * mm});
            skLineSegment(sketch, "E263.MirrorCS", {"start": v(3.12, -79.1) * mm, "end": v(3.12, -79.83) * mm});
            skArc(sketch, "E264.MirrorCS", {"start": v(8.3, -73.77) * mm, "mid": v(7.76, -74.34) * mm, "end": v(6.99, -74.14) * mm});
            skLineSegment(sketch, "E265.MirrorCS", {"start": v(15.1, -63.84) * mm, "end": v(15.1, -64.57) * mm});
            skLineSegment(sketch, "E266.MirrorCS", {"start": v(11.74, -62.34) * mm, "end": v(11.74, -62.83) * mm});
            skArc(sketch, "E267.MirrorCS", {"start": v(11.74, -62.34) * mm, "mid": v(11.9, -61.98) * mm, "end": v(12.25, -61.83) * mm});
            skArc(sketch, "E268.MirrorCS", {"start": v(15.1, -64.57) * mm, "mid": v(15.07, -64.76) * mm, "end": v(14.96, -64.93) * mm});
            skArc(sketch, "E269.MirrorCS", {"start": v(3.63, -80.33) * mm, "mid": v(3.27, -80.19) * mm, "end": v(3.12, -79.83) * mm});
            skArc(sketch, "E270.MirrorCS", {"start": v(12.25, -81.83) * mm, "mid": v(11.9, -81.69) * mm, "end": v(11.74, -81.33) * mm});
            skArc(sketch, "E271.MirrorCS", {"start": v(1.1, -63.33) * mm, "mid": v(1.47, -63.48) * mm, "end": v(1.62, -63.84) * mm});
            skArc(sketch, "E272.MirrorCS", {"start": v(3.12, -79.1) * mm, "mid": v(3.16, -78.9) * mm, "end": v(3.27, -78.74) * mm});
            skArc(sketch, "E273.MirrorCS", {"start": v(6.8, -73.96) * mm, "mid": v(6.6, -73.2) * mm, "end": v(7.18, -72.64) * mm});
            skLineSegment(sketch, "E274.MirrorCS", {"start": v(6.99, -69.53) * mm, "end": v(6.8, -69.7) * mm});
            skLineSegment(sketch, "E275.MirrorCS", {"start": v(6.48, -81.33) * mm, "end": v(6.48, -80.84) * mm});
            skArc(sketch, "E276.MirrorCS", {"start": v(6.48, -81.33) * mm, "mid": v(6.33, -81.69) * mm, "end": v(5.97, -81.83) * mm});
            skArc(sketch, "E277.MirrorCS", {"start": v(6.37, -75.64) * mm, "mid": v(6.53, -75.53) * mm, "end": v(6.73, -75.49) * mm});
            skLineSegment(sketch, "E278.MirrorCS", {"start": v(3.63, -63.33) * mm, "end": v(5.97, -63.33) * mm});
            skArc(sketch, "E279.MirrorCS", {"start": v(6.73, -68.18) * mm, "mid": v(6.53, -68.14) * mm, "end": v(6.37, -68.03) * mm});
            skArc(sketch, "E280.MirrorCS", {"start": v(11.05, -71.03) * mm, "mid": v(11.2, -71.83) * mm, "end": v(11.05, -72.64) * mm});
            skArc(sketch, "E281.MirrorCS", {"start": v(18.12, -69.2) * mm, "mid": v(17.76, -69.06) * mm, "end": v(17.61, -68.7) * mm});
            skArc(sketch, "E282.MirrorCS", {"start": v(1.62, -79.83) * mm, "mid": v(1.47, -80.19) * mm, "end": v(1.1, -80.33) * mm});
            skArc(sketch, "E283.MirrorCS", {"start": v(6.99, -69.53) * mm, "mid": v(7.76, -69.33) * mm, "end": v(8.3, -69.9) * mm});
            skArc(sketch, "E284.MirrorCS", {"start": v(17.61, -77.32) * mm, "mid": v(17.46, -77.68) * mm, "end": v(17.1, -77.83) * mm});
            skArc(sketch, "E285.MirrorCS", {"start": v(3.27, -64.93) * mm, "mid": v(3.16, -64.76) * mm, "end": v(3.12, -64.57) * mm});
            skArc(sketch, "E286.MirrorCS", {"start": v(11.74, -80.84) * mm, "mid": v(11.9, -80.48) * mm, "end": v(12.25, -80.33) * mm});
            skArc(sketch, "E287.MirrorCS", {"start": v(11.24, -74.14) * mm, "mid": v(10.47, -74.34) * mm, "end": v(9.92, -73.77) * mm});
            skArc(sketch, "E288.MirrorCS", {"start": v(17.1, -65.84) * mm, "mid": v(17.46, -65.99) * mm, "end": v(17.61, -66.35) * mm});
            skArc(sketch, "E289.MirrorCS", {"start": v(1.62, -78.48) * mm, "mid": v(1.66, -78.29) * mm, "end": v(1.77, -78.12) * mm});
            skLineSegment(sketch, "E290.MirrorCS", {"start": v(1.1, -63.33) * mm, "end": v(-0.89, -63.33) * mm});
            skArc(sketch, "E291.MirrorCS", {"start": v(17.61, -74.97) * mm, "mid": v(17.76, -74.61) * mm, "end": v(18.12, -74.46) * mm});
            skLineSegment(sketch, "E292.MirrorCS", {"start": v(18.6, -74.46) * mm, "end": v(18.12, -74.46) * mm});
            skArc(sketch, "E293.MirrorCS", {"start": v(3.12, -63.84) * mm, "mid": v(3.27, -63.48) * mm, "end": v(3.63, -63.33) * mm});
            skArc(sketch, "E294.MirrorCS", {"start": v(15.1, -79.83) * mm, "mid": v(14.96, -80.19) * mm, "end": v(14.6, -80.33) * mm});
            skArc(sketch, "E295.MirrorCS", {"start": v(16.02, -65.99) * mm, "mid": v(16.18, -65.88) * mm, "end": v(16.38, -65.84) * mm});
            skLineSegment(sketch, "E296.MirrorCS", {"start": v(17.61, -77.32) * mm, "end": v(17.61, -74.97) * mm});
            skLineSegment(sketch, "E297.MirrorCS", {"start": v(1.62, -63.84) * mm, "end": v(1.62, -65.2) * mm});
            skArc(sketch, "E298.MirrorCS", {"start": v(18.6, -74.46) * mm, "mid": v(18.96, -74.61) * mm, "end": v(19.11, -74.97) * mm});
            skLineSegment(sketch, "E299.MirrorCS", {"start": v(18.12, -69.2) * mm, "end": v(18.6, -69.2) * mm});
            skLineSegment(sketch, "E300.MirrorCS", {"start": v(16.38, -65.84) * mm, "end": v(17.1, -65.84) * mm});
            skArc(sketch, "E301.MirrorCS", {"start": v(12.25, -63.33) * mm, "mid": v(11.9, -63.19) * mm, "end": v(11.74, -62.83) * mm});
            skArc(sketch, "E302.MirrorCS", {"start": v(17.61, -61.83) * mm, "mid": v(18.67, -62.27) * mm, "end": v(19.11, -63.33) * mm});
            skArc(sketch, "E303.MirrorCS", {"start": v(14.6, -63.33) * mm, "mid": v(14.96, -63.48) * mm, "end": v(15.1, -63.84) * mm});
            skArc(sketch, "E304.MirrorCS", {"start": v(1.77, -65.55) * mm, "mid": v(1.66, -65.38) * mm, "end": v(1.62, -65.2) * mm});
            skArc(sketch, "E305.MirrorCS", {"start": v(6.48, -62.83) * mm, "mid": v(6.33, -63.19) * mm, "end": v(5.97, -63.33) * mm});
            skArc(sketch, "E306.MirrorCS", {"start": v(8.3, -69.9) * mm, "mid": v(9.11, -69.74) * mm, "end": v(9.92, -69.9) * mm});
            skArc(sketch, "E307.MirrorCS", {"start": v(9.92, -73.77) * mm, "mid": v(9.11, -73.93) * mm, "end": v(8.3, -73.77) * mm});
            skLineSegment(sketch, "E308.MirrorCS", {"start": v(16.38, -77.83) * mm, "end": v(17.1, -77.83) * mm});
            skArc(sketch, "E309.MirrorCS", {"start": v(5.97, -61.83) * mm, "mid": v(6.33, -61.98) * mm, "end": v(6.48, -62.34) * mm});
            skArc(sketch, "E310.MirrorCS", {"start": v(19.11, -80.33) * mm, "mid": v(18.67, -81.4) * mm, "end": v(17.61, -81.83) * mm});
            skArc(sketch, "E311.MirrorCS", {"start": v(9.92, -69.9) * mm, "mid": v(10.47, -69.33) * mm, "end": v(11.24, -69.53) * mm});
            skArc(sketch, "E312.MirrorCS", {"start": v(5.46, -74.22) * mm, "mid": v(5.42, -74.41) * mm, "end": v(5.3, -74.58) * mm});
            skLineSegment(sketch, "E313.MirrorCS", {"start": v(15.1, -79.1) * mm, "end": v(15.1, -79.83) * mm});
            skArc(sketch, "E314.MirrorCS", {"start": v(11.5, -75.49) * mm, "mid": v(11.7, -75.53) * mm, "end": v(11.86, -75.64) * mm});
            skLineSegment(sketch, "E315.MirrorCS", {"start": v(6.48, -62.83) * mm, "end": v(6.48, -62.34) * mm});
            skArc(sketch, "E316.MirrorCS", {"start": v(12.77, -69.45) * mm, "mid": v(12.8, -69.26) * mm, "end": v(12.92, -69.1) * mm});
            skArc(sketch, "E317.MirrorCS", {"start": v(12.92, -74.58) * mm, "mid": v(12.8, -74.41) * mm, "end": v(12.77, -74.22) * mm});
            skLineSegment(sketch, "E318.MirrorCS", {"start": v(11.24, -74.14) * mm, "end": v(11.42, -73.96) * mm});
            skArc(sketch, "E319.MirrorCS", {"start": v(11.42, -69.7) * mm, "mid": v(11.62, -70.48) * mm, "end": v(11.05, -71.03) * mm});
            skArc(sketch, "E320.MirrorCS", {"start": v(7.18, -71.03) * mm, "mid": v(6.6, -70.48) * mm, "end": v(6.8, -69.7) * mm});
            skLineSegment(sketch, "E321.MirrorCS", {"start": v(1.62, -78.48) * mm, "end": v(1.62, -79.83) * mm});
            skArc(sketch, "E322.MirrorCS", {"start": v(14.96, -78.74) * mm, "mid": v(15.07, -78.9) * mm, "end": v(15.1, -79.1) * mm});
            skLineSegment(sketch, "E323.MirrorCS", {"start": v(3.12, -63.84) * mm, "end": v(3.12, -64.57) * mm});
            skArc(sketch, "E324.MirrorCS", {"start": v(11.86, -68.03) * mm, "mid": v(11.7, -68.14) * mm, "end": v(11.5, -68.18) * mm});
            skArc(sketch, "E325.MirrorCS", {"start": v(5.97, -80.33) * mm, "mid": v(6.33, -80.48) * mm, "end": v(6.48, -80.84) * mm});
            skArc(sketch, "E326.MirrorCS", {"start": v(11.05, -72.64) * mm, "mid": v(11.62, -73.2) * mm, "end": v(11.42, -73.96) * mm});
            skArc(sketch, "E327.MirrorCS", {"start": v(19.11, -68.7) * mm, "mid": v(18.96, -69.06) * mm, "end": v(18.6, -69.2) * mm});
            skLineSegment(sketch, "E328.MirrorCS", {"start": v(-0.89, -80.33) * mm, "end": v(1.1, -80.33) * mm});
            skArc(sketch, "E329.MirrorCS", {"start": v(7.18, -72.64) * mm, "mid": v(7.02, -71.83) * mm, "end": v(7.18, -71.03) * mm});
            skLineSegment(sketch, "E330.MirrorCS", {"start": v(3.63, -80.33) * mm, "end": v(5.97, -80.33) * mm});
            skArc(sketch, "E331.MirrorCS", {"start": v(16.38, -77.83) * mm, "mid": v(16.18, -77.8) * mm, "end": v(16.02, -77.68) * mm});
            skLineSegment(sketch, "E332.MirrorCS", {"start": v(6.37, -75.64) * mm, "end": v(3.27, -78.74) * mm});
            skLineSegment(sketch, "E333.MirrorCS", {"start": v(5.46, -69.45) * mm, "end": v(5.46, -74.22) * mm});
            skLineSegment(sketch, "E334.MirrorCS", {"start": v(6.37, -68.03) * mm, "end": v(3.27, -64.93) * mm});
            skLineSegment(sketch, "E335.MirrorCS", {"start": v(11.5, -75.49) * mm, "end": v(6.73, -75.49) * mm});
            skLineSegment(sketch, "E336.MirrorCS", {"start": v(17.61, -66.35) * mm, "end": v(17.61, -68.7) * mm});
            skLineSegment(sketch, "E337.MirrorCS", {"start": v(12.92, -69.1) * mm, "end": v(16.02, -65.99) * mm});
            skLineSegment(sketch, "E338.MirrorCS", {"start": v(11.5, -68.18) * mm, "end": v(6.73, -68.18) * mm});
            skLineSegment(sketch, "E339.MirrorCS", {"start": v(14.96, -64.93) * mm, "end": v(11.86, -68.03) * mm});
            skLineSegment(sketch, "E340.MirrorCS", {"start": v(12.25, -63.33) * mm, "end": v(14.6, -63.33) * mm});
            skLineSegment(sketch, "E341.MirrorCS", {"start": v(17.61, -61.83) * mm, "end": v(12.25, -61.83) * mm});
            skLineSegment(sketch, "E342.MirrorCS", {"start": v(19.11, -68.7) * mm, "end": v(19.11, -63.33) * mm});
            skLineSegment(sketch, "E343.MirrorCS", {"start": v(5.3, -69.1) * mm, "end": v(1.77, -65.55) * mm});
            skLineSegment(sketch, "E344.MirrorCS", {"start": v(19.11, -80.33) * mm, "end": v(19.11, -74.97) * mm});
            skLineSegment(sketch, "E345.MirrorCS", {"start": v(5.97, -61.83) * mm, "end": v(-0.89, -61.83) * mm});
            skLineSegment(sketch, "E346.MirrorCS", {"start": v(17.61, -81.83) * mm, "end": v(12.25, -81.83) * mm});
            skLineSegment(sketch, "E347.MirrorCS", {"start": v(12.92, -74.58) * mm, "end": v(16.02, -77.68) * mm});
            skLineSegment(sketch, "E348.MirrorCS", {"start": v(14.96, -78.74) * mm, "end": v(11.86, -75.64) * mm});
            skLineSegment(sketch, "E349.MirrorCS", {"start": v(5.97, -81.83) * mm, "end": v(-0.89, -81.83) * mm});
            skLineSegment(sketch, "E350.MirrorCS", {"start": v(12.77, -69.45) * mm, "end": v(12.77, -74.22) * mm});
            skLineSegment(sketch, "E351.MirrorCS", {"start": v(12.25, -80.33) * mm, "end": v(14.6, -80.33) * mm});
            skLineSegment(sketch, "E352.MirrorCS", {"start": v(5.3, -74.58) * mm, "end": v(1.77, -78.12) * mm});
            skArc(sketch, "E353", {"start": v(-7.08, -69.1) * mm, "mid": v(-7.2, -69.26) * mm, "end": v(-7.23, -69.45) * mm});
            skArc(sketch, "E354", {"start": v(5.46, -69.45) * mm, "mid": v(5.42, -69.26) * mm, "end": v(5.3, -69.1) * mm});
            skLineSegment(sketch, "E355.bottom", {"start": v(58.92, 432.96) * mm, "end": v(558.92, 432.96) * mm});
            skLineSegment(sketch, "E355.top", {"start": v(58.92, -122.04) * mm, "end": v(558.92, -122.04) * mm});
            skLineSegment(sketch, "E355.left", {"start": v(58.92, 432.96) * mm, "end": v(58.92, -122.04) * mm});
            skLineSegment(sketch, "E355.right", {"start": v(558.92, 432.96) * mm, "end": v(558.92, -122.04) * mm});
            skSolve(sketch);
        }
        {
            var Q0;
            Q0=makeQuery(id+"F0.imprint","IMPRINT",FACE,{"disambiguationData":[TD([[makeQuery(id+"F0.imprint","IMPRINT",EDGE,{"derivedFrom":sQuery(id+"F0.wireOp",EDGE,"E0")}),1.0]])]});
            var Q1;
            Q1=makeQuery(id+"F0.imprint","IMPRINT",FACE,{"disambiguationData":[TD([[makeQuery(id+"F0.imprint","IMPRINT",EDGE,{"derivedFrom":sQuery(id+"F0.wireOp",EDGE,"E177")}),1.0]])]});
            extrude(context, id + "F1", {"entities" : qUnion([Q0, Q1]), "depth" : 500 * mm});
        }
        {
            var Q0;
            Q0=makeQuery(id+"F0.imprint","IMPRINT",FACE,{"disambiguationData":[TD([[makeQuery(id+"F0.imprint","IMPRINT",EDGE,{"derivedFrom":sQuery(id+"F0.wireOp",EDGE,"E0")}),1.0]])]});
            extrude(context, id + "F2", {"entities" : qUnion([Q0]), "depth" : 190 * mm});
        }
        {
            var Q0;
            Q0=makeQuery(id+"F0.imprint","IMPRINT",FACE,{"disambiguationData":[TD([[makeQuery(id+"F0.imprint","IMPRINT",EDGE,{"derivedFrom":sQuery(id+"F0.wireOp",EDGE,"E355.bottom")}),-1.0]])]});
            extrude(context, id + "F3", {"entities" : qUnion([Q0]), "depth" : 20 * mm});
        }
    });
